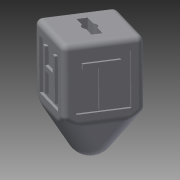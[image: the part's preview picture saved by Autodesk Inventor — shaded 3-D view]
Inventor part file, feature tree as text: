
AUTODESK INVENTOR PART (.ipt)
format: ipt  version: 2015 (Build 190159000, 159)  size: 372,224 bytes
history: native  units: in
note: dims shown in document units (in); Inventor stores cm internally (conversion verified against a paired STEP export)
features: extrude x13, sketch x13, projected_geometry x8, fillet x4
ambient origin geometry x8: Origin, YZ Plane, XZ Plane, XY Plane, X Axis, Y Axis, Z Axis, Center Point
bodies: Solid1 (feature_tree)
feature tree (38):
  extrude  "Extrusion1"  Depth=1.5in
  extrude  "Extrusion2"  Depth=0.25in
  extrude  "Extrusion3"  Depth=0.0625in
  fillet  "Fillet1"  Radius=0.4375in
  fillet  "Fillet2"  Radius=0.125in
  fillet  "Fillet3"  Radius=0.125in
  fillet  "Fillet4"  Radius=0.0625in
  extrude  "Extrusion4"  Depth=0.125in
  extrude  "Extrusion5"  Depth=0.125in
  extrude  "Extrusion6"  Depth=0.0625in TaperAngle=0.0deg
  extrude  "Extrusion7"  Depth=0.125in
  extrude  "Extrusion8"  Depth=0.125in
  extrude  "Extrusion9"  Depth=0.0625in TaperAngle=0.0deg
  extrude  "Extrusion10"  Depth=0.0625in TaperAngle=0.0deg
  extrude  "Extrusion11"  Depth=0.0625in TaperAngle=0.0deg
  extrude  "Extrusion12"  Depth=0.0625in TaperAngle=0.0deg
  extrude  "Extrusion13"  Depth=0.1in
  sketch  "Sketch1"  dims[d0=1.5in d1=1.5in]
  sketch  "Sketch2"  dims[d2=1.5in d3=0.0in d4=0.25in]
  sketch  "Sketch3"  dims[d5=1.25in d6=0.0in d7=1.3125in d8=-0.2061in d9=0.4375in d10=0.25in d11=0.125in d12=0.125in d13=0.0625in]
  projected_geometry  "Projected Loop1"
  sketch  "Sketch4"  dims[d14=0.125in d15=0.125in]
  projected_geometry  "Projected Loop2"
  sketch  "Sketch5"  dims[d16=0.125in d17=0.125in]
  projected_geometry  "Projected Loop3"
  sketch  "Sketch6"  dims[d18=0.125in d19=0.0625in d20=0.0in]
  projected_geometry  "Projected Loop4"
  sketch  "Sketch7"  dims[d21=0.0625in d22=0.0in d23=0.125in]
  projected_geometry  "Projected Loop5"
  sketch  "Sketch8"  dims[d24=0.125in d25=0.125in]
  projected_geometry  "Projected Loop6"
  sketch  "Sketch9"  dims[d26=0.125in d27=0.0625in d28=0.0in]
  projected_geometry  "Projected Loop7"
  sketch  "Sketch10"  dims[d29=0.0625in d30=0.0in d31=0.0625in d32=0.0in]
  sketch  "Sketch11"  dims[d33=0.0625in d34=0.0in d35=0.0625in d36=0.0in]
  projected_geometry  "Projected Loop8"
  sketch  "Sketch12"  dims[d37=0.0625in d38=0.0in d42=1.0in d43=0.0in]
  sketch  "Sketch13"  dims[d44=0.3in d47=0.1in d48=0.1in d49=0.4in d50=0.75in d51=0.0in]
